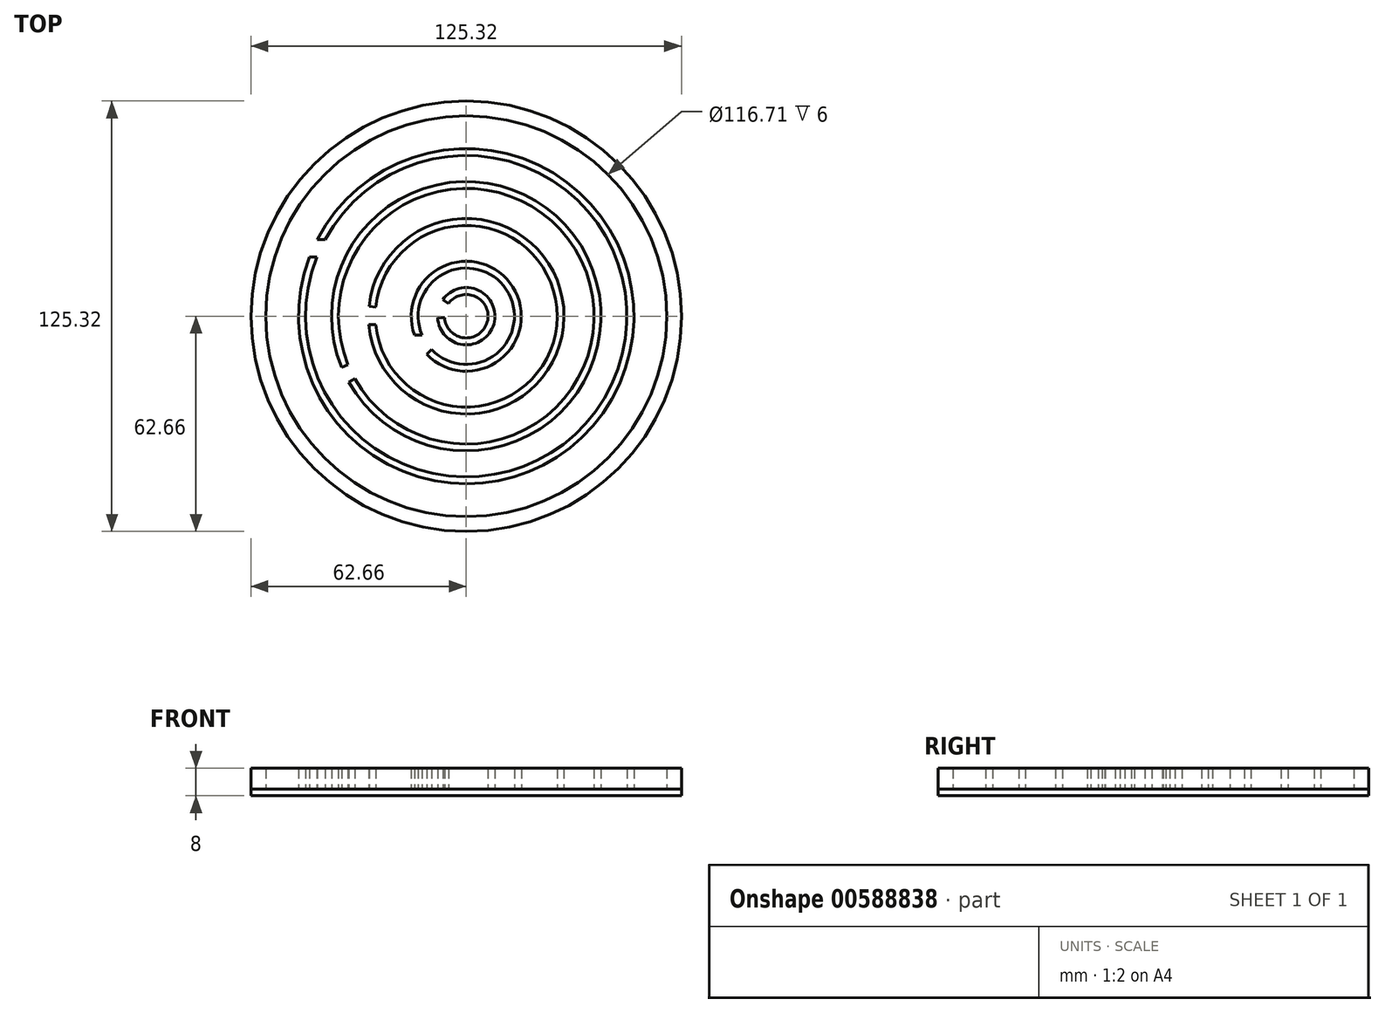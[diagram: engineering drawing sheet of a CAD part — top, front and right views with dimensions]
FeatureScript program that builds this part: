
annotation { "Feature Type Name" : "Feature", "Feature Type Description" : "" }
export const myFeature = defineFeature(function(context is Context, id is Id, definition is map)
    precondition{}
    {
        {
            var Q0;
            Q0=qCreatedBy(makeId("Top.planeOp"),FACE);
            var sketch = newSketch(context, id + "F0", { "sketchPlane" : qUnion([Q0])});
            skCircle(sketch, "E0", {"center": v(0, 0) * mm, "radius": 58.36 * mm});
            skCircle(sketch, "E1.0", {"center": v(0, 0) * mm, "radius": 62.66 * mm});
            skArc(sketch, "E2.0", {"start": v(-6.32, -0.46) * mm, "mid": v(6.1, -1.7) * mm, "end": v(-5.18, 3.65) * mm});
            skArc(sketch, "E3.0", {"start": v(-8.32, -0.46) * mm, "mid": v(8.01, -2.3) * mm, "end": v(-6.81, 4.8) * mm});
            skLineSegment(sketch, "E4", {"start": v(-5.18, 3.65) * mm, "end": v(-6.81, 4.8) * mm});
            skArc(sketch, "E5.0", {"start": v(-28.35, -2.44) * mm, "mid": v(28.45, -0.2) * mm, "end": v(-28.3, 2.85) * mm});
            skLineSegment(sketch, "E6", {"start": v(-28.3, 2.85) * mm, "end": v(-26.32, 2.65) * mm});
            skArc(sketch, "E7", {"start": v(-11.5, -11.13) * mm, "mid": v(13.57, 8.5) * mm, "end": v(-15.04, -5.49) * mm});
            skArc(sketch, "E8.0", {"start": v(-10.07, -9.74) * mm, "mid": v(11.68, 7.74) * mm, "end": v(-12.9, -5.49) * mm});
            skLineSegment(sketch, "E9", {"start": v(-11.5, -11.13) * mm, "end": v(-10.07, -9.74) * mm});
            skArc(sketch, "E10", {"start": v(-34.17, -19.2) * mm, "mid": v(35.3, 17.07) * mm, "end": v(-36.27, -14.86) * mm});
            skArc(sketch, "E11.0", {"start": v(-32.43, -18.23) * mm, "mid": v(33.5, 16.2) * mm, "end": v(-34.42, -14.1) * mm});
            skLineSegment(sketch, "E12", {"start": v(-36.27, -14.86) * mm, "end": v(-34.42, -14.1) * mm});
            skLineSegment(sketch, "E13", {"start": v(-34.17, -19.2) * mm, "end": v(-32.43, -18.23) * mm});
            skLineSegment(sketch, "E14.bottom", {"start": v(-8.32, -0.46) * mm, "end": v(-6.32, -0.46) * mm});
            skLineSegment(sketch, "E15.bottom", {"start": v(-15.04, -5.49) * mm, "end": v(-12.9, -5.49) * mm});
            skLineSegment(sketch, "E16.top", {"start": v(-28.43, -2.44) * mm, "end": v(-26.34, -2.44) * mm});
            skArc(sketch, "E17.trimOffspring", {"start": v(-26.34, -2.44) * mm, "mid": v(26.45, -0.1) * mm, "end": v(-26.32, 2.65) * mm});
            skArc(sketch, "E18", {"start": v(-45.65, 17.2) * mm, "mid": v(44.6, -19.77) * mm, "end": v(-43.4, 22.28) * mm});
            skArc(sketch, "E19.0", {"start": v(-43.5, 17.2) * mm, "mid": v(42.4, -19.77) * mm, "end": v(-41.13, 22.28) * mm});
            skLineSegment(sketch, "E20.bottom", {"start": v(-43.4, 22.28) * mm, "end": v(-41.13, 22.28) * mm});
            skLineSegment(sketch, "E20.top", {"start": v(-45.65, 17.2) * mm, "end": v(-43.5, 17.2) * mm});
            skPoint(sketch, "E21.0.midPoint", {"position": v(68.97, 0) * mm});
            skSolve(sketch);
        }
        {
            var Q0;
            Q0=makeQuery(id+"F0.imprint","IMPRINT",FACE,{"disambiguationData":[TD([[makeQuery(id+"F0.imprint","IMPRINT",EDGE,{"derivedFrom":sQuery(id+"F0.wireOp",EDGE,"E18")}),1.0]])]});
            var Q1;
            Q1=makeQuery(id+"F0.imprint","IMPRINT",FACE,{"disambiguationData":[TD([[makeQuery(id+"F0.imprint","IMPRINT",EDGE,{"derivedFrom":sQuery(id+"F0.wireOp",EDGE,"E0")}),-1.0]])]});
            var Q2;
            Q2=makeQuery(id+"F0.imprint","IMPRINT",FACE,{"disambiguationData":[TD([[makeQuery(id+"F0.imprint","IMPRINT",EDGE,{"derivedFrom":sQuery(id+"F0.wireOp",EDGE,"E10")}),1.0]])]});
            var Q3;
            {var subQ0=sQuery(id+"F0.wireOp",EDGE,"E5.0");Q3=makeQuery(id+"F0.imprint","IMPRINT",FACE,{"disambiguationData":[TD([[makeQuery(id+"F0.imprint","IMPRINT",EDGE,{"derivedFrom":subQ0}),1.0]])]});}
            var Q4;
            Q4=makeQuery(id+"F0.imprint","IMPRINT",FACE,{"disambiguationData":[TD([[makeQuery(id+"F0.imprint","IMPRINT",EDGE,{"derivedFrom":sQuery(id+"F0.wireOp",EDGE,"E7")}),1.0]])]});
            var Q5;
            Q5=makeQuery(id+"F0.imprint","IMPRINT",FACE,{"disambiguationData":[TD([[makeQuery(id+"F0.imprint","IMPRINT",EDGE,{"derivedFrom":sQuery(id+"F0.wireOp",EDGE,"E2.0")}),-1.0]])]});
            extrude(context, id + "F1", {"entities" : qUnion([Q0, Q1, Q2, Q3, Q4, Q5]), "depth" : 6 * mm, "offsetDistance" : 25 * mm});
        }
        {
            var Q0;
            Q0=qCreatedBy(makeId("Top.planeOp"),FACE);
            var sketch = newSketch(context, id + "F2", { "sketchPlane" : qUnion([Q0])});
            skCircle(sketch, "E22.0", {"center": v(0, 0) * mm, "radius": 62.66 * mm});
            skSolve(sketch);
        }
        {
            var Q0;
            Q0 = qSketchRegion(id + "F2", true);
            extrude(context, id + "F3", {"entities" : qUnion([Q0]), "oppositeDirection" : true, "depth" : 2 * mm, "offsetDistance" : 25 * mm});
        }
    });
